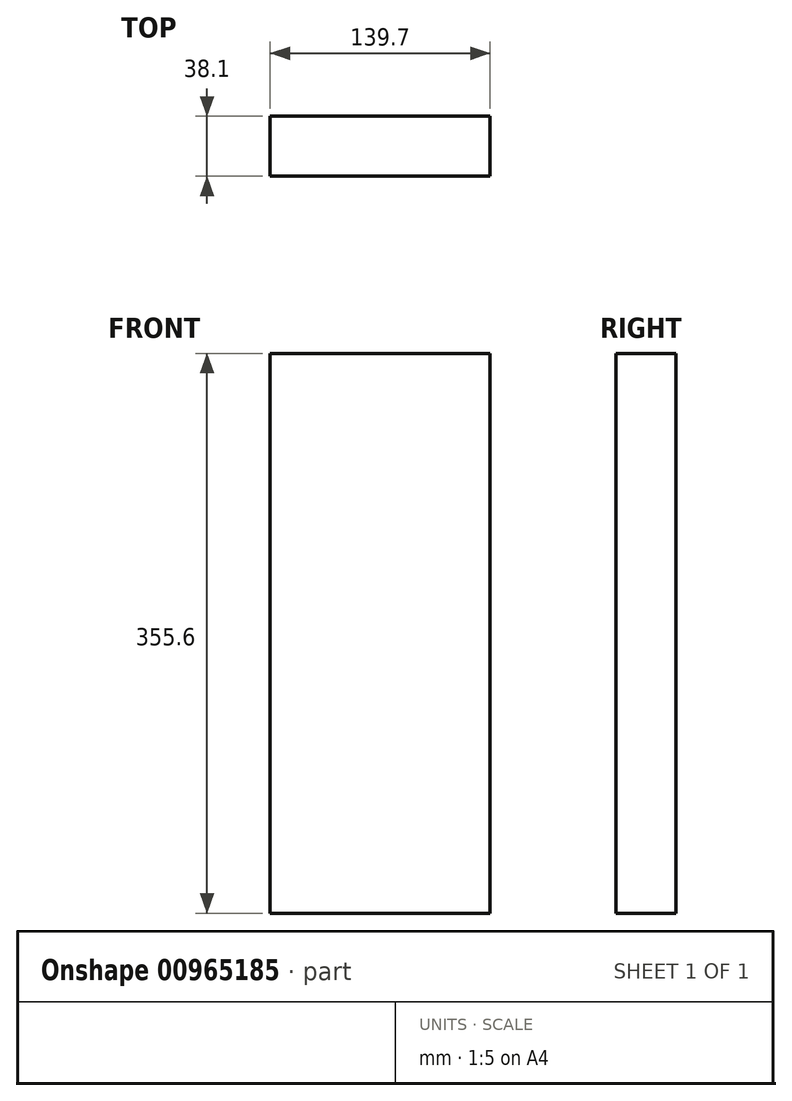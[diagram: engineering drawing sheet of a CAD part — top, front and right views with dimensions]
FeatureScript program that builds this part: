
annotation { "Feature Type Name" : "Feature", "Feature Type Description" : "" }
export const myFeature = defineFeature(function(context is Context, id is Id, definition is map)
    precondition{}
    {
        {
            var Q0;
            Q0=qCreatedBy(makeId("Top.planeOp"),FACE);
            var sketch = newSketch(context, id + "F0", { "sketchPlane" : qUnion([Q0])});
            skLineSegment(sketch, "E0.bottom", {"start": v(-23.73, 95.26) * mm, "end": v(115.97, 95.26) * mm});
            skLineSegment(sketch, "E0.top", {"start": v(-23.73, 133.36) * mm, "end": v(115.97, 133.36) * mm});
            skLineSegment(sketch, "E0.left", {"start": v(-23.73, 95.26) * mm, "end": v(-23.73, 133.36) * mm});
            skLineSegment(sketch, "E0.right", {"start": v(115.97, 95.26) * mm, "end": v(115.97, 133.36) * mm});
            skSolve(sketch);
        }
        {
            var Q0;
            Q0=makeQuery(id+"F0.imprint","IMPRINT",FACE,{"disambiguationData":[TD([[makeQuery(id+"F0.imprint","IMPRINT",EDGE,{"derivedFrom":sQuery(id+"F0.wireOp",EDGE,"E0.bottom")}),1.0]])]});
            extrude(context, id + "F1", {"entities" : qUnion([Q0]), "depth" : 355.6 * mm, "offsetDistance" : 25.4 * mm});
        }
    });
